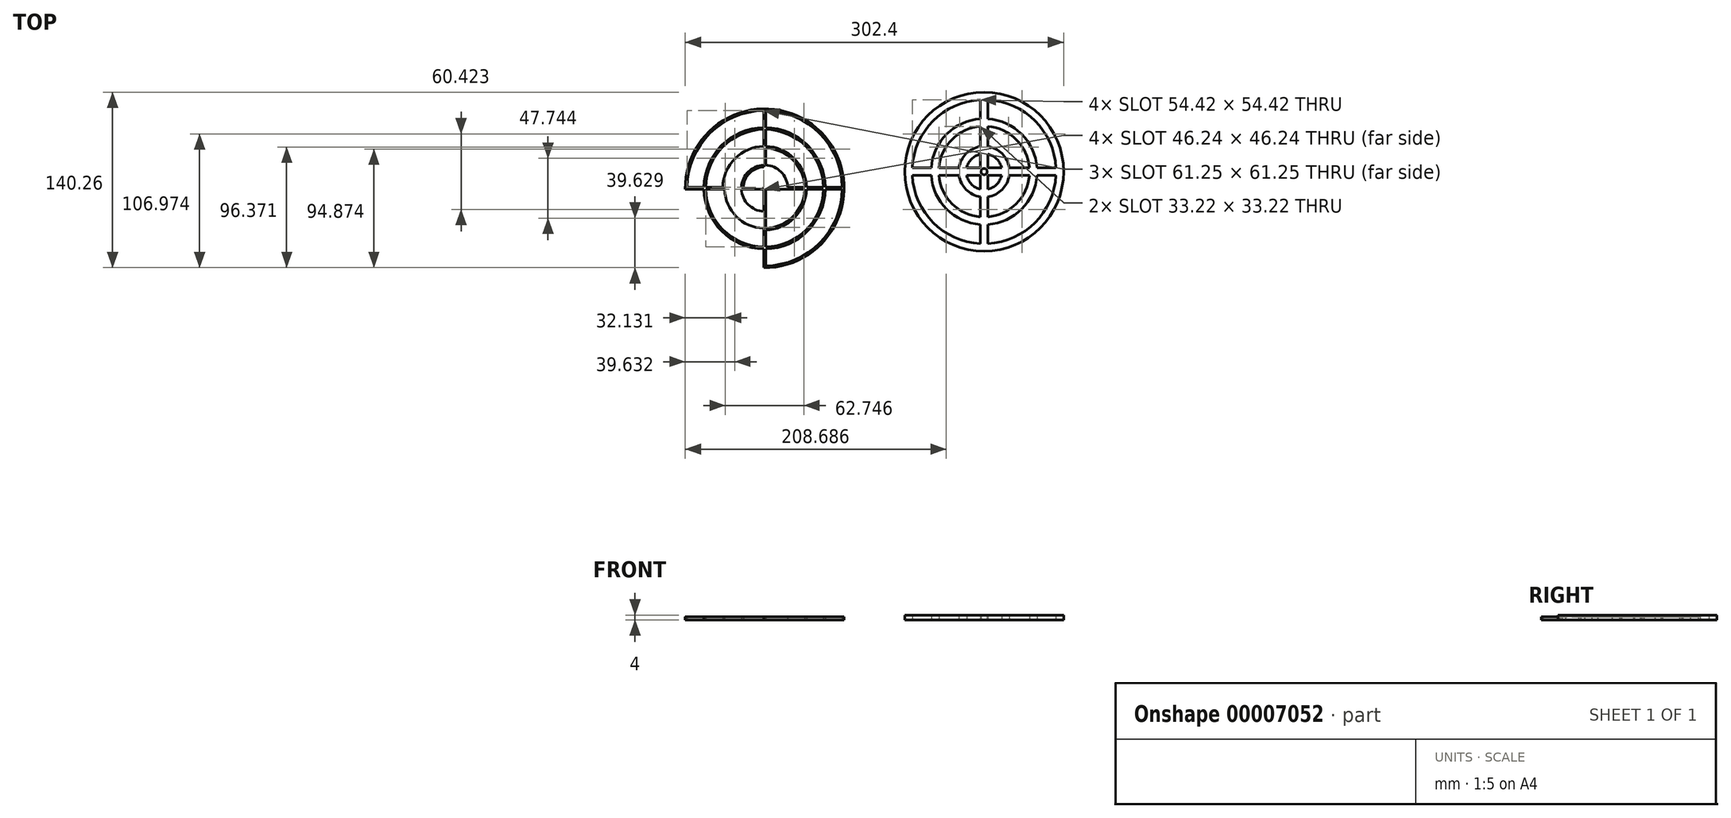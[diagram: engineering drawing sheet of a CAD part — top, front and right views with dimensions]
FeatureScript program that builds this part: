
annotation { "Feature Type Name" : "Feature", "Feature Type Description" : "" }
export const myFeature = defineFeature(function(context is Context, id is Id, definition is map)
    precondition{}
    {
        {
            var Q0;
            Q0=qCreatedBy(makeId("Top.planeOp"),FACE);
            var sketch = newSketch(context, id + "F0", { "sketchPlane" : qUnion([Q0])});
            skLineSegment(sketch, "E0.bottom", {"start": v(-96.22, 91.83) * mm, "end": v(30.78, 91.83) * mm});
            skLineSegment(sketch, "E0.top", {"start": v(-96.22, -35.17) * mm, "end": v(30.78, -35.17) * mm});
            skLineSegment(sketch, "E0.left", {"start": v(-96.22, 91.83) * mm, "end": v(-96.22, -35.17) * mm});
            skLineSegment(sketch, "E0.right", {"start": v(30.78, 91.83) * mm, "end": v(30.78, -35.17) * mm});
            skCircle(sketch, "E1", {"center": v(-32.72, 28.33) * mm, "radius": 63.5 * mm});
            skLineSegment(sketch, "E2", {"start": v(-33.47, 91.83) * mm, "end": v(-33.47, -35.16) * mm});
            skLineSegment(sketch, "E3", {"start": v(-31.97, 91.83) * mm, "end": v(-31.97, -35.16) * mm});
            skLineSegment(sketch, "E4", {"start": v(30.78, 29.08) * mm, "end": v(-96.22, 29.08) * mm});
            skLineSegment(sketch, "E5", {"start": v(30.78, 27.58) * mm, "end": v(-96.22, 27.58) * mm});
            skCircle(sketch, "E6", {"center": v(-32.72, 28.33) * mm, "radius": 62 * mm});
            skCircle(sketch, "E7", {"center": v(-32.72, 28.33) * mm, "radius": 48.5 * mm});
            skCircle(sketch, "E8", {"center": v(-32.72, 28.33) * mm, "radius": 47 * mm});
            skCircle(sketch, "E9", {"center": v(-32.72, 28.33) * mm, "radius": 33.5 * mm});
            skCircle(sketch, "E10", {"center": v(-32.72, 28.33) * mm, "radius": 32 * mm});
            skCircle(sketch, "E11", {"center": v(-32.72, 28.33) * mm, "radius": 18.5 * mm});
            skCircle(sketch, "E12", {"center": v(-32.72, 28.33) * mm, "radius": 17 * mm});
            skLineSegment(sketch, "E13", {"start": v(30.78, -35.17) * mm, "end": v(79.18, -35.17) * mm});
            skLineSegment(sketch, "E14", {"start": v(79.18, -35.17) * mm, "end": v(79.18, 105.1) * mm});
            skLineSegment(sketch, "E15.bottom", {"start": v(79.18, 105.1) * mm, "end": v(206.18, 105.1) * mm});
            skLineSegment(sketch, "E15.top", {"start": v(79.18, -21.9) * mm, "end": v(206.18, -21.9) * mm});
            skLineSegment(sketch, "E15.left", {"start": v(79.18, 105.1) * mm, "end": v(79.18, -21.9) * mm});
            skLineSegment(sketch, "E15.right", {"start": v(206.18, 105.1) * mm, "end": v(206.18, -21.9) * mm});
            skCircle(sketch, "E16", {"center": v(142.68, 41.6) * mm, "radius": 63.5 * mm});
            skCircle(sketch, "E17", {"center": v(142.68, 41.6) * mm, "radius": 42.34 * mm});
            skCircle(sketch, "E18", {"center": v(142.68, 41.6) * mm, "radius": 36.34 * mm});
            skCircle(sketch, "E19", {"center": v(142.68, 41.6) * mm, "radius": 20.3 * mm});
            skCircle(sketch, "E20", {"center": v(142.68, 41.6) * mm, "radius": 14.3 * mm});
            skCircle(sketch, "E21", {"center": v(142.68, 41.6) * mm, "radius": 57.5 * mm});
            skCircle(sketch, "E22", {"center": v(142.68, 41.6) * mm, "radius": 2.5 * mm});
            skLineSegment(sketch, "E23", {"start": v(145.68, 44.6) * mm, "end": v(156.66, 44.6) * mm});
            skLineSegment(sketch, "E24", {"start": v(162.75, 44.6) * mm, "end": v(178.9, 44.6) * mm});
            skLineSegment(sketch, "E25", {"start": v(184.91, 44.6) * mm, "end": v(200.1, 44.6) * mm});
            skLineSegment(sketch, "E26", {"start": v(200.1, 38.59) * mm, "end": v(184.9, 38.59) * mm});
            skLineSegment(sketch, "E27", {"start": v(178.9, 38.59) * mm, "end": v(162.75, 38.59) * mm});
            skLineSegment(sketch, "E28", {"start": v(156.66, 38.59) * mm, "end": v(145.68, 38.59) * mm});
            skLineSegment(sketch, "E29", {"start": v(145.68, 44.6) * mm, "end": v(145.68, 55.58) * mm});
            skLineSegment(sketch, "E30", {"start": v(145.68, 61.67) * mm, "end": v(145.68, 77.8) * mm});
            skLineSegment(sketch, "E31", {"start": v(145.68, 83.83) * mm, "end": v(145.68, 99.01) * mm});
            skLineSegment(sketch, "E32", {"start": v(139.68, 99.01) * mm, "end": v(139.68, 83.83) * mm});
            skLineSegment(sketch, "E33", {"start": v(139.68, 77.8) * mm, "end": v(139.68, 61.67) * mm});
            skLineSegment(sketch, "E34", {"start": v(139.68, 55.58) * mm, "end": v(139.68, 44.6) * mm});
            skLineSegment(sketch, "E35", {"start": v(139.68, 44.6) * mm, "end": v(128.7, 44.6) * mm});
            skLineSegment(sketch, "E36", {"start": v(122.6, 44.6) * mm, "end": v(106.46, 44.6) * mm});
            skLineSegment(sketch, "E37", {"start": v(100.44, 44.6) * mm, "end": v(85.25, 44.6) * mm});
            skLineSegment(sketch, "E38", {"start": v(85.26, 38.59) * mm, "end": v(100.44, 38.59) * mm});
            skLineSegment(sketch, "E39", {"start": v(106.46, 38.59) * mm, "end": v(122.6, 38.59) * mm});
            skLineSegment(sketch, "E40", {"start": v(128.7, 38.59) * mm, "end": v(139.68, 38.59) * mm});
            skLineSegment(sketch, "E41", {"start": v(139.68, 38.59) * mm, "end": v(139.68, 27.61) * mm});
            skLineSegment(sketch, "E42", {"start": v(145.68, 38.59) * mm, "end": v(145.68, 27.61) * mm});
            skLineSegment(sketch, "E43", {"start": v(139.68, 21.52) * mm, "end": v(139.68, 5.38) * mm});
            skLineSegment(sketch, "E44", {"start": v(145.68, 21.52) * mm, "end": v(145.68, 5.38) * mm});
            skLineSegment(sketch, "E45", {"start": v(139.68, -0.64) * mm, "end": v(139.68, -15.83) * mm});
            skLineSegment(sketch, "E46", {"start": v(145.68, 0) * mm, "end": v(145.68, -15.83) * mm});
            skSolve(sketch);
        }
        {
            var Q0;
            {var subQ3=sQuery(id+"F0.wireOp",EDGE,"E2");var subQ5=sQuery(id+"F0.wireOp",EDGE,"E1");var subQ7=makeQuery(id+"F0.imprint","INTERSECT",VERTEX,{"disambiguationData":[OD(1.0)],"derivedFrom":[subQ5,subQ3]});Q0=makeQuery(id+"F0.imprint","IMPRINT",FACE,{"disambiguationData":[TD([[makeQuery(id+"F0.imprint","IMPRINT",EDGE,{"disambiguationData":[TD([[subQ7,-1.0]])],"derivedFrom":subQ5}),1.0]])]});}
            var Q1;
            {var subQ1=sQuery(id+"F0.wireOp",EDGE,"E3");var subQ5=sQuery(id+"F0.wireOp",EDGE,"E1");var subQ6=makeQuery(id+"F0.imprint","INTERSECT",VERTEX,{"disambiguationData":[OD(0.0)],"derivedFrom":[subQ5,subQ1]});Q1=makeQuery(id+"F0.imprint","IMPRINT",FACE,{"disambiguationData":[TD([[makeQuery(id+"F0.imprint","IMPRINT",EDGE,{"disambiguationData":[TD([[subQ6,-1.0]])],"derivedFrom":subQ5}),1.0]])]});}
            var Q2;
            {var subQ3=sQuery(id+"F0.wireOp",EDGE,"E3");var subQ5=sQuery(id+"F0.wireOp",EDGE,"E1");var subQ7=makeQuery(id+"F0.imprint","INTERSECT",VERTEX,{"disambiguationData":[OD(0.0)],"derivedFrom":[subQ5,subQ3]});Q2=makeQuery(id+"F0.imprint","IMPRINT",FACE,{"disambiguationData":[TD([[makeQuery(id+"F0.imprint","IMPRINT",EDGE,{"disambiguationData":[TD([[subQ7,1.0]])],"derivedFrom":subQ5}),1.0]])]});}
            var Q3;
            {var subQ3=sQuery(id+"F0.wireOp",EDGE,"E2");var subQ5=sQuery(id+"F0.wireOp",EDGE,"E6");var subQ7=makeQuery(id+"F0.imprint","INTERSECT",VERTEX,{"disambiguationData":[OD(0.0)],"derivedFrom":[subQ3,subQ5]});Q3=makeQuery(id+"F0.imprint","IMPRINT",FACE,{"disambiguationData":[TD([[makeQuery(id+"F0.imprint","IMPRINT",EDGE,{"disambiguationData":[TD([[subQ7,-1.0]])],"derivedFrom":subQ3}),1.0]])]});}
            var Q4;
            {var subQ3=sQuery(id+"F0.wireOp",EDGE,"E2");var subQ5=sQuery(id+"F0.wireOp",EDGE,"E7");var subQ7=makeQuery(id+"F0.imprint","INTERSECT",VERTEX,{"disambiguationData":[OD(0.0)],"derivedFrom":[subQ3,subQ5]});Q4=makeQuery(id+"F0.imprint","IMPRINT",FACE,{"disambiguationData":[TD([[makeQuery(id+"F0.imprint","IMPRINT",EDGE,{"disambiguationData":[TD([[subQ7,-1.0]])],"derivedFrom":subQ3}),1.0]])]});}
            var Q5;
            {var subQ3=sQuery(id+"F0.wireOp",EDGE,"E3");var subQ5=sQuery(id+"F0.wireOp",EDGE,"E7");var subQ7=makeQuery(id+"F0.imprint","INTERSECT",VERTEX,{"disambiguationData":[OD(0.0)],"derivedFrom":[subQ3,subQ5]});Q5=makeQuery(id+"F0.imprint","IMPRINT",FACE,{"disambiguationData":[TD([[makeQuery(id+"F0.imprint","IMPRINT",EDGE,{"disambiguationData":[TD([[subQ7,-1.0]])],"derivedFrom":subQ3}),1.0]])]});}
            var Q6;
            {var subQ3=sQuery(id+"F0.wireOp",EDGE,"E2");var subQ5=sQuery(id+"F0.wireOp",EDGE,"E7");var subQ7=makeQuery(id+"F0.imprint","INTERSECT",VERTEX,{"disambiguationData":[OD(0.0)],"derivedFrom":[subQ3,subQ5]});Q6=makeQuery(id+"F0.imprint","IMPRINT",FACE,{"disambiguationData":[TD([[makeQuery(id+"F0.imprint","IMPRINT",EDGE,{"disambiguationData":[TD([[subQ7,-1.0]])],"derivedFrom":subQ3}),-1.0]])]});}
            var Q7;
            {var subQ3=sQuery(id+"F0.wireOp",EDGE,"E2");var subQ5=sQuery(id+"F0.wireOp",EDGE,"E8");var subQ7=makeQuery(id+"F0.imprint","INTERSECT",VERTEX,{"disambiguationData":[OD(0.0)],"derivedFrom":[subQ3,subQ5]});Q7=makeQuery(id+"F0.imprint","IMPRINT",FACE,{"disambiguationData":[TD([[makeQuery(id+"F0.imprint","IMPRINT",EDGE,{"disambiguationData":[TD([[subQ7,-1.0]])],"derivedFrom":subQ3}),1.0]])]});}
            var Q8;
            {var subQ3=sQuery(id+"F0.wireOp",EDGE,"E2");var subQ5=sQuery(id+"F0.wireOp",EDGE,"E9");var subQ7=makeQuery(id+"F0.imprint","INTERSECT",VERTEX,{"disambiguationData":[OD(0.0)],"derivedFrom":[subQ3,subQ5]});Q8=makeQuery(id+"F0.imprint","IMPRINT",FACE,{"disambiguationData":[TD([[makeQuery(id+"F0.imprint","IMPRINT",EDGE,{"disambiguationData":[TD([[subQ7,-1.0]])],"derivedFrom":subQ3}),-1.0]])]});}
            var Q9;
            {var subQ0=sQuery(id+"F0.wireOp",EDGE,"E9");var subQ3=sQuery(id+"F0.wireOp",EDGE,"E2");var subQ4=makeQuery(id+"F0.imprint","INTERSECT",VERTEX,{"disambiguationData":[OD(0.0)],"derivedFrom":[subQ3,subQ0]});Q9=makeQuery(id+"F0.imprint","IMPRINT",FACE,{"disambiguationData":[TD([[makeQuery(id+"F0.imprint","IMPRINT",EDGE,{"disambiguationData":[TD([[subQ4,-1.0]])],"derivedFrom":subQ3}),1.0]])]});}
            var Q10;
            {var subQ3=sQuery(id+"F0.wireOp",EDGE,"E3");var subQ5=sQuery(id+"F0.wireOp",EDGE,"E9");var subQ7=makeQuery(id+"F0.imprint","INTERSECT",VERTEX,{"disambiguationData":[OD(0.0)],"derivedFrom":[subQ3,subQ5]});Q10=makeQuery(id+"F0.imprint","IMPRINT",FACE,{"disambiguationData":[TD([[makeQuery(id+"F0.imprint","IMPRINT",EDGE,{"disambiguationData":[TD([[subQ7,-1.0]])],"derivedFrom":subQ3}),1.0]])]});}
            var Q11;
            {var subQ0=sQuery(id+"F0.wireOp",EDGE,"E10");var subQ3=sQuery(id+"F0.wireOp",EDGE,"E2");var subQ4=makeQuery(id+"F0.imprint","INTERSECT",VERTEX,{"disambiguationData":[OD(0.0)],"derivedFrom":[subQ3,subQ0]});Q11=makeQuery(id+"F0.imprint","IMPRINT",FACE,{"disambiguationData":[TD([[makeQuery(id+"F0.imprint","IMPRINT",EDGE,{"disambiguationData":[TD([[subQ4,-1.0]])],"derivedFrom":subQ3}),1.0]])]});}
            var Q12;
            {var subQ3=sQuery(id+"F0.wireOp",EDGE,"E2");var subQ5=sQuery(id+"F0.wireOp",EDGE,"E11");var subQ7=makeQuery(id+"F0.imprint","INTERSECT",VERTEX,{"disambiguationData":[OD(0.0)],"derivedFrom":[subQ3,subQ5]});Q12=makeQuery(id+"F0.imprint","IMPRINT",FACE,{"disambiguationData":[TD([[makeQuery(id+"F0.imprint","IMPRINT",EDGE,{"disambiguationData":[TD([[subQ7,-1.0]])],"derivedFrom":subQ3}),1.0]])]});}
            var Q13;
            {var subQ0=sQuery(id+"F0.wireOp",EDGE,"E12");var subQ3=sQuery(id+"F0.wireOp",EDGE,"E2");var subQ4=makeQuery(id+"F0.imprint","INTERSECT",VERTEX,{"disambiguationData":[OD(0.0)],"derivedFrom":[subQ3,subQ0]});Q13=makeQuery(id+"F0.imprint","IMPRINT",FACE,{"disambiguationData":[TD([[makeQuery(id+"F0.imprint","IMPRINT",EDGE,{"disambiguationData":[TD([[subQ4,-1.0]])],"derivedFrom":subQ3}),1.0]])]});}
            var Q14;
            {var subQ3=sQuery(id+"F0.wireOp",EDGE,"E3");var subQ5=sQuery(id+"F0.wireOp",EDGE,"E11");var subQ7=makeQuery(id+"F0.imprint","INTERSECT",VERTEX,{"disambiguationData":[OD(0.0)],"derivedFrom":[subQ3,subQ5]});Q14=makeQuery(id+"F0.imprint","IMPRINT",FACE,{"disambiguationData":[TD([[makeQuery(id+"F0.imprint","IMPRINT",EDGE,{"disambiguationData":[TD([[subQ7,-1.0]])],"derivedFrom":subQ3}),1.0]])]});}
            var Q15;
            {var subQ3=sQuery(id+"F0.wireOp",EDGE,"E2");var subQ5=sQuery(id+"F0.wireOp",EDGE,"E11");var subQ7=makeQuery(id+"F0.imprint","INTERSECT",VERTEX,{"disambiguationData":[OD(0.0)],"derivedFrom":[subQ3,subQ5]});Q15=makeQuery(id+"F0.imprint","IMPRINT",FACE,{"disambiguationData":[TD([[makeQuery(id+"F0.imprint","IMPRINT",EDGE,{"disambiguationData":[TD([[subQ7,-1.0]])],"derivedFrom":subQ3}),-1.0]])]});}
            var Q16;
            {var subQ3=sQuery(id+"F0.wireOp",EDGE,"E4");var subQ5=sQuery(id+"F0.wireOp",EDGE,"E2");var subQ7=makeQuery(id+"F0.imprint","INTERSECT",VERTEX,{"derivedFrom":[subQ5,subQ3]});Q16=makeQuery(id+"F0.imprint","IMPRINT",FACE,{"disambiguationData":[TD([[makeQuery(id+"F0.imprint","IMPRINT",EDGE,{"disambiguationData":[TD([[subQ7,-1.0]])],"derivedFrom":subQ5}),-1.0]])]});}
            var Q17;
            {var subQ3=sQuery(id+"F0.wireOp",EDGE,"E4");var subQ5=sQuery(id+"F0.wireOp",EDGE,"E3");var subQ7=makeQuery(id+"F0.imprint","INTERSECT",VERTEX,{"derivedFrom":[subQ5,subQ3]});Q17=makeQuery(id+"F0.imprint","IMPRINT",FACE,{"disambiguationData":[TD([[makeQuery(id+"F0.imprint","IMPRINT",EDGE,{"disambiguationData":[TD([[subQ7,-1.0]])],"derivedFrom":subQ5}),1.0]])]});}
            var Q18;
            {var subQ3=sQuery(id+"F0.wireOp",EDGE,"E4");var subQ5=sQuery(id+"F0.wireOp",EDGE,"E11");var subQ7=makeQuery(id+"F0.imprint","INTERSECT",VERTEX,{"disambiguationData":[OD(0.0)],"derivedFrom":[subQ3,subQ5]});Q18=makeQuery(id+"F0.imprint","IMPRINT",FACE,{"disambiguationData":[TD([[makeQuery(id+"F0.imprint","IMPRINT",EDGE,{"disambiguationData":[TD([[subQ7,-1.0]])],"derivedFrom":subQ3}),1.0]])]});}
            var Q19;
            {var subQ3=sQuery(id+"F0.wireOp",EDGE,"E2");var subQ5=sQuery(id+"F0.wireOp",EDGE,"E4");var subQ7=makeQuery(id+"F0.imprint","INTERSECT",VERTEX,{"derivedFrom":[subQ3,subQ5]});Q19=makeQuery(id+"F0.imprint","IMPRINT",FACE,{"disambiguationData":[TD([[makeQuery(id+"F0.imprint","IMPRINT",EDGE,{"disambiguationData":[TD([[subQ7,-1.0]])],"derivedFrom":subQ3}),1.0]])]});}
            var Q20;
            {var subQ3=sQuery(id+"F0.wireOp",EDGE,"E4");var subQ5=sQuery(id+"F0.wireOp",EDGE,"E10");var subQ7=makeQuery(id+"F0.imprint","INTERSECT",VERTEX,{"disambiguationData":[OD(0.0)],"derivedFrom":[subQ3,subQ5]});Q20=makeQuery(id+"F0.imprint","IMPRINT",FACE,{"disambiguationData":[TD([[makeQuery(id+"F0.imprint","IMPRINT",EDGE,{"disambiguationData":[TD([[subQ7,-1.0]])],"derivedFrom":subQ3}),1.0]])]});}
            var Q21;
            {var subQ3=sQuery(id+"F0.wireOp",EDGE,"E4");var subQ5=sQuery(id+"F0.wireOp",EDGE,"E9");var subQ7=makeQuery(id+"F0.imprint","INTERSECT",VERTEX,{"disambiguationData":[OD(0.0)],"derivedFrom":[subQ3,subQ5]});Q21=makeQuery(id+"F0.imprint","IMPRINT",FACE,{"disambiguationData":[TD([[makeQuery(id+"F0.imprint","IMPRINT",EDGE,{"disambiguationData":[TD([[subQ7,-1.0]])],"derivedFrom":subQ3}),1.0]])]});}
            var Q22;
            {var subQ3=sQuery(id+"F0.wireOp",EDGE,"E4");var subQ5=sQuery(id+"F0.wireOp",EDGE,"E8");var subQ7=makeQuery(id+"F0.imprint","INTERSECT",VERTEX,{"disambiguationData":[OD(0.0)],"derivedFrom":[subQ3,subQ5]});Q22=makeQuery(id+"F0.imprint","IMPRINT",FACE,{"disambiguationData":[TD([[makeQuery(id+"F0.imprint","IMPRINT",EDGE,{"disambiguationData":[TD([[subQ7,-1.0]])],"derivedFrom":subQ3}),1.0]])]});}
            var Q23;
            {var subQ3=sQuery(id+"F0.wireOp",EDGE,"E4");var subQ5=sQuery(id+"F0.wireOp",EDGE,"E7");var subQ7=makeQuery(id+"F0.imprint","INTERSECT",VERTEX,{"disambiguationData":[OD(0.0)],"derivedFrom":[subQ3,subQ5]});Q23=makeQuery(id+"F0.imprint","IMPRINT",FACE,{"disambiguationData":[TD([[makeQuery(id+"F0.imprint","IMPRINT",EDGE,{"disambiguationData":[TD([[subQ7,-1.0]])],"derivedFrom":subQ3}),1.0]])]});}
            var Q24;
            {var subQ3=sQuery(id+"F0.wireOp",EDGE,"E4");var subQ5=sQuery(id+"F0.wireOp",EDGE,"E6");var subQ7=makeQuery(id+"F0.imprint","INTERSECT",VERTEX,{"disambiguationData":[OD(0.0)],"derivedFrom":[subQ3,subQ5]});Q24=makeQuery(id+"F0.imprint","IMPRINT",FACE,{"disambiguationData":[TD([[makeQuery(id+"F0.imprint","IMPRINT",EDGE,{"disambiguationData":[TD([[subQ7,-1.0]])],"derivedFrom":subQ3}),1.0]])]});}
            var Q25;
            {var subQ0=sQuery(id+"F0.wireOp",EDGE,"E8");var subQ3=sQuery(id+"F0.wireOp",EDGE,"E3");var subQ4=makeQuery(id+"F0.imprint","INTERSECT",VERTEX,{"disambiguationData":[OD(1.0)],"derivedFrom":[subQ3,subQ0]});Q25=makeQuery(id+"F0.imprint","IMPRINT",FACE,{"disambiguationData":[TD([[makeQuery(id+"F0.imprint","IMPRINT",EDGE,{"disambiguationData":[TD([[subQ4,-1.0]])],"derivedFrom":subQ3}),1.0]])]});}
            var Q26;
            {var subQ3=sQuery(id+"F0.wireOp",EDGE,"E3");var subQ5=sQuery(id+"F0.wireOp",EDGE,"E12");var subQ7=makeQuery(id+"F0.imprint","INTERSECT",VERTEX,{"disambiguationData":[OD(1.0)],"derivedFrom":[subQ3,subQ5]});Q26=makeQuery(id+"F0.imprint","IMPRINT",FACE,{"disambiguationData":[TD([[makeQuery(id+"F0.imprint","IMPRINT",EDGE,{"disambiguationData":[TD([[subQ7,-1.0]])],"derivedFrom":subQ3}),1.0]])]});}
            var Q27;
            {var subQ0=sQuery(id+"F0.wireOp",EDGE,"E10");var subQ3=sQuery(id+"F0.wireOp",EDGE,"E3");var subQ4=makeQuery(id+"F0.imprint","INTERSECT",VERTEX,{"disambiguationData":[OD(1.0)],"derivedFrom":[subQ3,subQ0]});Q27=makeQuery(id+"F0.imprint","IMPRINT",FACE,{"disambiguationData":[TD([[makeQuery(id+"F0.imprint","IMPRINT",EDGE,{"disambiguationData":[TD([[subQ4,-1.0]])],"derivedFrom":subQ3}),1.0]])]});}
            var Q28;
            {var subQ5=sQuery(id+"F0.wireOp",EDGE,"E1");var subQ8=makeQuery(id+"F0.imprint","INTERSECT",VERTEX,{"derivedFrom":[sQuery(id+"F0.wireOp",EDGE,"E0.right"),subQ5]});Q28=makeQuery(id+"F0.imprint","IMPRINT",FACE,{"disambiguationData":[TD([[makeQuery(id+"F0.imprint","IMPRINT",EDGE,{"disambiguationData":[TD([[subQ8,-1.0]])],"derivedFrom":subQ5}),1.0]])]});}
            var Q29;
            {var subQ3=sQuery(id+"F0.wireOp",EDGE,"E3");var subQ5=sQuery(id+"F0.wireOp",EDGE,"E1");var subQ7=makeQuery(id+"F0.imprint","INTERSECT",VERTEX,{"disambiguationData":[OD(1.0)],"derivedFrom":[subQ5,subQ3]});Q29=makeQuery(id+"F0.imprint","IMPRINT",FACE,{"disambiguationData":[TD([[makeQuery(id+"F0.imprint","IMPRINT",EDGE,{"disambiguationData":[TD([[subQ7,-1.0]])],"derivedFrom":subQ5}),1.0]])]});}
            var Q30;
            {var subQ3=sQuery(id+"F0.wireOp",EDGE,"E2");var subQ5=sQuery(id+"F0.wireOp",EDGE,"E5");var subQ7=makeQuery(id+"F0.imprint","INTERSECT",VERTEX,{"derivedFrom":[subQ3,subQ5]});Q30=makeQuery(id+"F0.imprint","IMPRINT",FACE,{"disambiguationData":[TD([[makeQuery(id+"F0.imprint","IMPRINT",EDGE,{"disambiguationData":[TD([[subQ7,-1.0]])],"derivedFrom":subQ3}),1.0]])]});}
            var Q31;
            {var subQ0=sQuery(id+"F0.wireOp",EDGE,"E12");var subQ3=sQuery(id+"F0.wireOp",EDGE,"E2");var subQ4=makeQuery(id+"F0.imprint","INTERSECT",VERTEX,{"disambiguationData":[OD(1.0)],"derivedFrom":[subQ3,subQ0]});Q31=makeQuery(id+"F0.imprint","IMPRINT",FACE,{"disambiguationData":[TD([[makeQuery(id+"F0.imprint","IMPRINT",EDGE,{"disambiguationData":[TD([[subQ4,-1.0]])],"derivedFrom":subQ3}),1.0]])]});}
            var Q32;
            {var subQ0=sQuery(id+"F0.wireOp",EDGE,"E11");var subQ3=sQuery(id+"F0.wireOp",EDGE,"E2");var subQ4=makeQuery(id+"F0.imprint","INTERSECT",VERTEX,{"disambiguationData":[OD(1.0)],"derivedFrom":[subQ3,subQ0]});Q32=makeQuery(id+"F0.imprint","IMPRINT",FACE,{"disambiguationData":[TD([[makeQuery(id+"F0.imprint","IMPRINT",EDGE,{"disambiguationData":[TD([[subQ4,-1.0]])],"derivedFrom":subQ3}),1.0]])]});}
            var Q33;
            {var subQ0=sQuery(id+"F0.wireOp",EDGE,"E10");var subQ3=sQuery(id+"F0.wireOp",EDGE,"E2");var subQ4=makeQuery(id+"F0.imprint","INTERSECT",VERTEX,{"disambiguationData":[OD(1.0)],"derivedFrom":[subQ3,subQ0]});Q33=makeQuery(id+"F0.imprint","IMPRINT",FACE,{"disambiguationData":[TD([[makeQuery(id+"F0.imprint","IMPRINT",EDGE,{"disambiguationData":[TD([[subQ4,-1.0]])],"derivedFrom":subQ3}),1.0]])]});}
            var Q34;
            {var subQ0=sQuery(id+"F0.wireOp",EDGE,"E10");var subQ3=sQuery(id+"F0.wireOp",EDGE,"E2");var subQ4=makeQuery(id+"F0.imprint","INTERSECT",VERTEX,{"disambiguationData":[OD(1.0)],"derivedFrom":[subQ3,subQ0]});Q34=makeQuery(id+"F0.imprint","IMPRINT",FACE,{"disambiguationData":[TD([[makeQuery(id+"F0.imprint","IMPRINT",EDGE,{"disambiguationData":[TD([[subQ4,-1.0]])],"derivedFrom":subQ3}),-1.0]])]});}
            var Q35;
            {var subQ0=sQuery(id+"F0.wireOp",EDGE,"E9");var subQ3=sQuery(id+"F0.wireOp",EDGE,"E2");var subQ4=makeQuery(id+"F0.imprint","INTERSECT",VERTEX,{"disambiguationData":[OD(1.0)],"derivedFrom":[subQ3,subQ0]});Q35=makeQuery(id+"F0.imprint","IMPRINT",FACE,{"disambiguationData":[TD([[makeQuery(id+"F0.imprint","IMPRINT",EDGE,{"disambiguationData":[TD([[subQ4,-1.0]])],"derivedFrom":subQ3}),1.0]])]});}
            var Q36;
            {var subQ0=sQuery(id+"F0.wireOp",EDGE,"E8");var subQ3=sQuery(id+"F0.wireOp",EDGE,"E2");var subQ4=makeQuery(id+"F0.imprint","INTERSECT",VERTEX,{"disambiguationData":[OD(1.0)],"derivedFrom":[subQ3,subQ0]});Q36=makeQuery(id+"F0.imprint","IMPRINT",FACE,{"disambiguationData":[TD([[makeQuery(id+"F0.imprint","IMPRINT",EDGE,{"disambiguationData":[TD([[subQ4,-1.0]])],"derivedFrom":subQ3}),-1.0]])]});}
            var Q37;
            {var subQ0=sQuery(id+"F0.wireOp",EDGE,"E8");var subQ3=sQuery(id+"F0.wireOp",EDGE,"E2");var subQ4=makeQuery(id+"F0.imprint","INTERSECT",VERTEX,{"disambiguationData":[OD(1.0)],"derivedFrom":[subQ3,subQ0]});Q37=makeQuery(id+"F0.imprint","IMPRINT",FACE,{"disambiguationData":[TD([[makeQuery(id+"F0.imprint","IMPRINT",EDGE,{"disambiguationData":[TD([[subQ4,-1.0]])],"derivedFrom":subQ3}),1.0]])]});}
            var Q38;
            {var subQ0=sQuery(id+"F0.wireOp",EDGE,"E7");var subQ3=sQuery(id+"F0.wireOp",EDGE,"E2");var subQ4=makeQuery(id+"F0.imprint","INTERSECT",VERTEX,{"disambiguationData":[OD(1.0)],"derivedFrom":[subQ3,subQ0]});Q38=makeQuery(id+"F0.imprint","IMPRINT",FACE,{"disambiguationData":[TD([[makeQuery(id+"F0.imprint","IMPRINT",EDGE,{"disambiguationData":[TD([[subQ4,-1.0]])],"derivedFrom":subQ3}),1.0]])]});}
            var Q39;
            {var subQ3=sQuery(id+"F0.wireOp",EDGE,"E2");var subQ5=sQuery(id+"F0.wireOp",EDGE,"E1");var subQ7=makeQuery(id+"F0.imprint","INTERSECT",VERTEX,{"disambiguationData":[OD(0.0)],"derivedFrom":[subQ5,subQ3]});Q39=makeQuery(id+"F0.imprint","IMPRINT",FACE,{"disambiguationData":[TD([[makeQuery(id+"F0.imprint","IMPRINT",EDGE,{"disambiguationData":[TD([[subQ7,1.0]])],"derivedFrom":subQ5}),1.0]])]});}
            var Q40;
            {var subQ3=sQuery(id+"F0.wireOp",EDGE,"E2");var subQ5=sQuery(id+"F0.wireOp",EDGE,"E1");var subQ7=makeQuery(id+"F0.imprint","INTERSECT",VERTEX,{"disambiguationData":[OD(0.0)],"derivedFrom":[subQ5,subQ3]});Q40=makeQuery(id+"F0.imprint","IMPRINT",FACE,{"disambiguationData":[TD([[makeQuery(id+"F0.imprint","IMPRINT",EDGE,{"disambiguationData":[TD([[subQ7,-1.0]])],"derivedFrom":subQ5}),1.0]])]});}
            var Q41;
            {var subQ0=sQuery(id+"F0.wireOp",EDGE,"E12");var subQ3=sQuery(id+"F0.wireOp",EDGE,"E4");var subQ4=makeQuery(id+"F0.imprint","INTERSECT",VERTEX,{"disambiguationData":[OD(1.0)],"derivedFrom":[subQ3,subQ0]});Q41=makeQuery(id+"F0.imprint","IMPRINT",FACE,{"disambiguationData":[TD([[makeQuery(id+"F0.imprint","IMPRINT",EDGE,{"disambiguationData":[TD([[subQ4,-1.0]])],"derivedFrom":subQ3}),1.0]])]});}
            var Q42;
            {var subQ0=sQuery(id+"F0.wireOp",EDGE,"E12");var subQ3=sQuery(id+"F0.wireOp",EDGE,"E2");var subQ4=makeQuery(id+"F0.imprint","INTERSECT",VERTEX,{"disambiguationData":[OD(1.0)],"derivedFrom":[subQ3,subQ0]});Q42=makeQuery(id+"F0.imprint","IMPRINT",FACE,{"disambiguationData":[TD([[makeQuery(id+"F0.imprint","IMPRINT",EDGE,{"disambiguationData":[TD([[subQ4,-1.0]])],"derivedFrom":subQ3}),-1.0]])]});}
            var Q43;
            {var subQ0=sQuery(id+"F0.wireOp",EDGE,"E11");var subQ3=sQuery(id+"F0.wireOp",EDGE,"E4");var subQ4=makeQuery(id+"F0.imprint","INTERSECT",VERTEX,{"disambiguationData":[OD(1.0)],"derivedFrom":[subQ3,subQ0]});Q43=makeQuery(id+"F0.imprint","IMPRINT",FACE,{"disambiguationData":[TD([[makeQuery(id+"F0.imprint","IMPRINT",EDGE,{"disambiguationData":[TD([[subQ4,-1.0]])],"derivedFrom":subQ3}),1.0]])]});}
            var Q44;
            {var subQ3=sQuery(id+"F0.wireOp",EDGE,"E4");var subQ5=sQuery(id+"F0.wireOp",EDGE,"E10");var subQ7=makeQuery(id+"F0.imprint","INTERSECT",VERTEX,{"disambiguationData":[OD(1.0)],"derivedFrom":[subQ3,subQ5]});Q44=makeQuery(id+"F0.imprint","IMPRINT",FACE,{"disambiguationData":[TD([[makeQuery(id+"F0.imprint","IMPRINT",EDGE,{"disambiguationData":[TD([[subQ7,-1.0]])],"derivedFrom":subQ3}),1.0]])]});}
            var Q45;
            {var subQ0=sQuery(id+"F0.wireOp",EDGE,"E9");var subQ3=sQuery(id+"F0.wireOp",EDGE,"E4");var subQ4=makeQuery(id+"F0.imprint","INTERSECT",VERTEX,{"disambiguationData":[OD(1.0)],"derivedFrom":[subQ3,subQ0]});Q45=makeQuery(id+"F0.imprint","IMPRINT",FACE,{"disambiguationData":[TD([[makeQuery(id+"F0.imprint","IMPRINT",EDGE,{"disambiguationData":[TD([[subQ4,-1.0]])],"derivedFrom":subQ3}),1.0]])]});}
            var Q46;
            {var subQ3=sQuery(id+"F0.wireOp",EDGE,"E4");var subQ5=sQuery(id+"F0.wireOp",EDGE,"E8");var subQ7=makeQuery(id+"F0.imprint","INTERSECT",VERTEX,{"disambiguationData":[OD(1.0)],"derivedFrom":[subQ3,subQ5]});Q46=makeQuery(id+"F0.imprint","IMPRINT",FACE,{"disambiguationData":[TD([[makeQuery(id+"F0.imprint","IMPRINT",EDGE,{"disambiguationData":[TD([[subQ7,-1.0]])],"derivedFrom":subQ3}),1.0]])]});}
            var Q47;
            {var subQ0=sQuery(id+"F0.wireOp",EDGE,"E7");var subQ3=sQuery(id+"F0.wireOp",EDGE,"E4");var subQ4=makeQuery(id+"F0.imprint","INTERSECT",VERTEX,{"disambiguationData":[OD(1.0)],"derivedFrom":[subQ3,subQ0]});Q47=makeQuery(id+"F0.imprint","IMPRINT",FACE,{"disambiguationData":[TD([[makeQuery(id+"F0.imprint","IMPRINT",EDGE,{"disambiguationData":[TD([[subQ4,-1.0]])],"derivedFrom":subQ3}),1.0]])]});}
            var Q48;
            {var subQ5=sQuery(id+"F0.wireOp",EDGE,"E1");var subQ8=makeQuery(id+"F0.imprint","INTERSECT",VERTEX,{"derivedFrom":[sQuery(id+"F0.wireOp",EDGE,"E0.left"),subQ5]});Q48=makeQuery(id+"F0.imprint","IMPRINT",FACE,{"disambiguationData":[TD([[makeQuery(id+"F0.imprint","IMPRINT",EDGE,{"disambiguationData":[TD([[subQ8,1.0]])],"derivedFrom":subQ5}),1.0]])]});}
            extrude(context, id + "F1", {"entities" : qUnion([Q0, Q1, Q2, Q3, Q4, Q5, Q6, Q7, Q8, Q9, Q10, Q11, Q12, Q13, Q14, Q15, Q16, Q17, Q18, Q19, Q20, Q21, Q22, Q23, Q24, Q25, Q26, Q27, Q28, Q29, Q30, Q31, Q32, Q33, Q34, Q35, Q36, Q37, Q38, Q39, Q40, Q41, Q42, Q43, Q44, Q45, Q46, Q47, Q48]), "depth" : 2.5 * mm});
        }
        {
            var Q0;
            {var subQ2=sQuery(id+"F0.wireOp",EDGE,"E31");Q0=makeQuery(id+"F0.imprint","IMPRINT",FACE,{"disambiguationData":[TD([[makeQuery(id+"F0.imprint","IMPRINT",EDGE,{"derivedFrom":subQ2}),1.0]])]});}
            var Q1;
            {var subQ9=sQuery(id+"F0.wireOp",EDGE,"E16");var subQ13=makeQuery(id+"F0.imprint","INTERSECT",VERTEX,{"derivedFrom":[sQuery(id+"F0.wireOp",EDGE,"E15.bottom"),subQ9]});Q1=makeQuery(id+"F0.imprint","IMPRINT",FACE,{"disambiguationData":[TD([[makeQuery(id+"F0.imprint","IMPRINT",EDGE,{"disambiguationData":[TD([[subQ13,1.0]])],"derivedFrom":subQ9}),1.0]])]});}
            var Q2;
            {var subQ8=sQuery(id+"F0.wireOp",EDGE,"E17");var subQ17=makeQuery(id+"F0.imprint","INTERSECT",VERTEX,{"derivedFrom":[subQ8,sQuery(id+"F0.wireOp",EDGE,"E25")]});Q2=makeQuery(id+"F0.imprint","IMPRINT",FACE,{"disambiguationData":[TD([[makeQuery(id+"F0.imprint","IMPRINT",EDGE,{"disambiguationData":[TD([[subQ17,-1.0]])],"derivedFrom":subQ8}),1.0]])]});}
            var Q3;
            {var subQ1=sQuery(id+"F0.wireOp",EDGE,"E30");Q3=makeQuery(id+"F0.imprint","IMPRINT",FACE,{"disambiguationData":[TD([[makeQuery(id+"F0.imprint","IMPRINT",EDGE,{"derivedFrom":subQ1}),1.0]])]});}
            var Q4;
            {var subQ7=sQuery(id+"F0.wireOp",EDGE,"E19");var subQ17=makeQuery(id+"F0.imprint","INTERSECT",VERTEX,{"derivedFrom":[subQ7,sQuery(id+"F0.wireOp",EDGE,"E24")]});Q4=makeQuery(id+"F0.imprint","IMPRINT",FACE,{"disambiguationData":[TD([[makeQuery(id+"F0.imprint","IMPRINT",EDGE,{"disambiguationData":[TD([[subQ17,-1.0]])],"derivedFrom":subQ7}),1.0]])]});}
            var Q5;
            {var subQ1=sQuery(id+"F0.wireOp",EDGE,"E24");Q5=makeQuery(id+"F0.imprint","IMPRINT",FACE,{"disambiguationData":[TD([[makeQuery(id+"F0.imprint","IMPRINT",EDGE,{"derivedFrom":subQ1}),-1.0]])]});}
            var Q6;
            {var subQ1=sQuery(id+"F0.wireOp",EDGE,"E25");Q6=makeQuery(id+"F0.imprint","IMPRINT",FACE,{"disambiguationData":[TD([[makeQuery(id+"F0.imprint","IMPRINT",EDGE,{"derivedFrom":subQ1}),-1.0]])]});}
            var Q7;
            Q7=makeQuery(id+"F0.imprint","IMPRINT",FACE,{"disambiguationData":[TD([[makeQuery(id+"F0.imprint","IMPRINT",EDGE,{"derivedFrom":sQuery(id+"F0.wireOp",EDGE,"E22")}),-1.0]])]});
            var Q8;
            {var subQ0=sQuery(id+"F0.wireOp",EDGE,"E43");Q8=makeQuery(id+"F0.imprint","IMPRINT",FACE,{"disambiguationData":[TD([[makeQuery(id+"F0.imprint","IMPRINT",EDGE,{"derivedFrom":subQ0}),1.0]])]});}
            var Q9;
            {var subQ5=sQuery(id+"F0.wireOp",EDGE,"E45");Q9=makeQuery(id+"F0.imprint","IMPRINT",FACE,{"disambiguationData":[TD([[makeQuery(id+"F0.imprint","IMPRINT",EDGE,{"derivedFrom":subQ5}),1.0]])]});}
            var Q10;
            {var subQ1=sQuery(id+"F0.wireOp",EDGE,"E36");Q10=makeQuery(id+"F0.imprint","IMPRINT",FACE,{"disambiguationData":[TD([[makeQuery(id+"F0.imprint","IMPRINT",EDGE,{"derivedFrom":subQ1}),1.0]])]});}
            var Q11;
            {var subQ2=sQuery(id+"F0.wireOp",EDGE,"E37");Q11=makeQuery(id+"F0.imprint","IMPRINT",FACE,{"disambiguationData":[TD([[makeQuery(id+"F0.imprint","IMPRINT",EDGE,{"derivedFrom":subQ2}),1.0]])]});}
            extrude(context, id + "F2", {"entities" : qUnion([Q0, Q1, Q2, Q3, Q4, Q5, Q6, Q7, Q8, Q9, Q10, Q11]), "depth" : 4 * mm});
        }
    });
